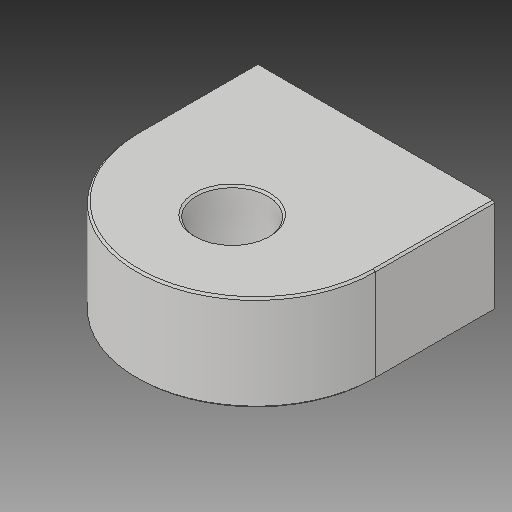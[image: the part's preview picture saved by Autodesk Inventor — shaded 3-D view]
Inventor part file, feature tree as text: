
AUTODESK INVENTOR PART (.ipt)
format: ipt  version: 2018 (Build 220112000, 112)  size: 107,008 bytes
history: native  units: in
note: dims shown in document units (in); Inventor stores cm internally (conversion verified against a paired STEP export)
features: chamfer x1
ambient origin geometry x8: Origin, YZ Plane, XZ Plane, XY Plane, X Axis, Y Axis, Z Axis, Center Point
bodies: Solid1 (feature_tree)
feature tree (1):
  chamfer  "Chamfer1"  [1 undecoded]
note: 1 required parameter value undecoded (feature->parameter linkage not recoverable at this tier; creation-order binding heuristic only, values carry confidence <= 0.55)
